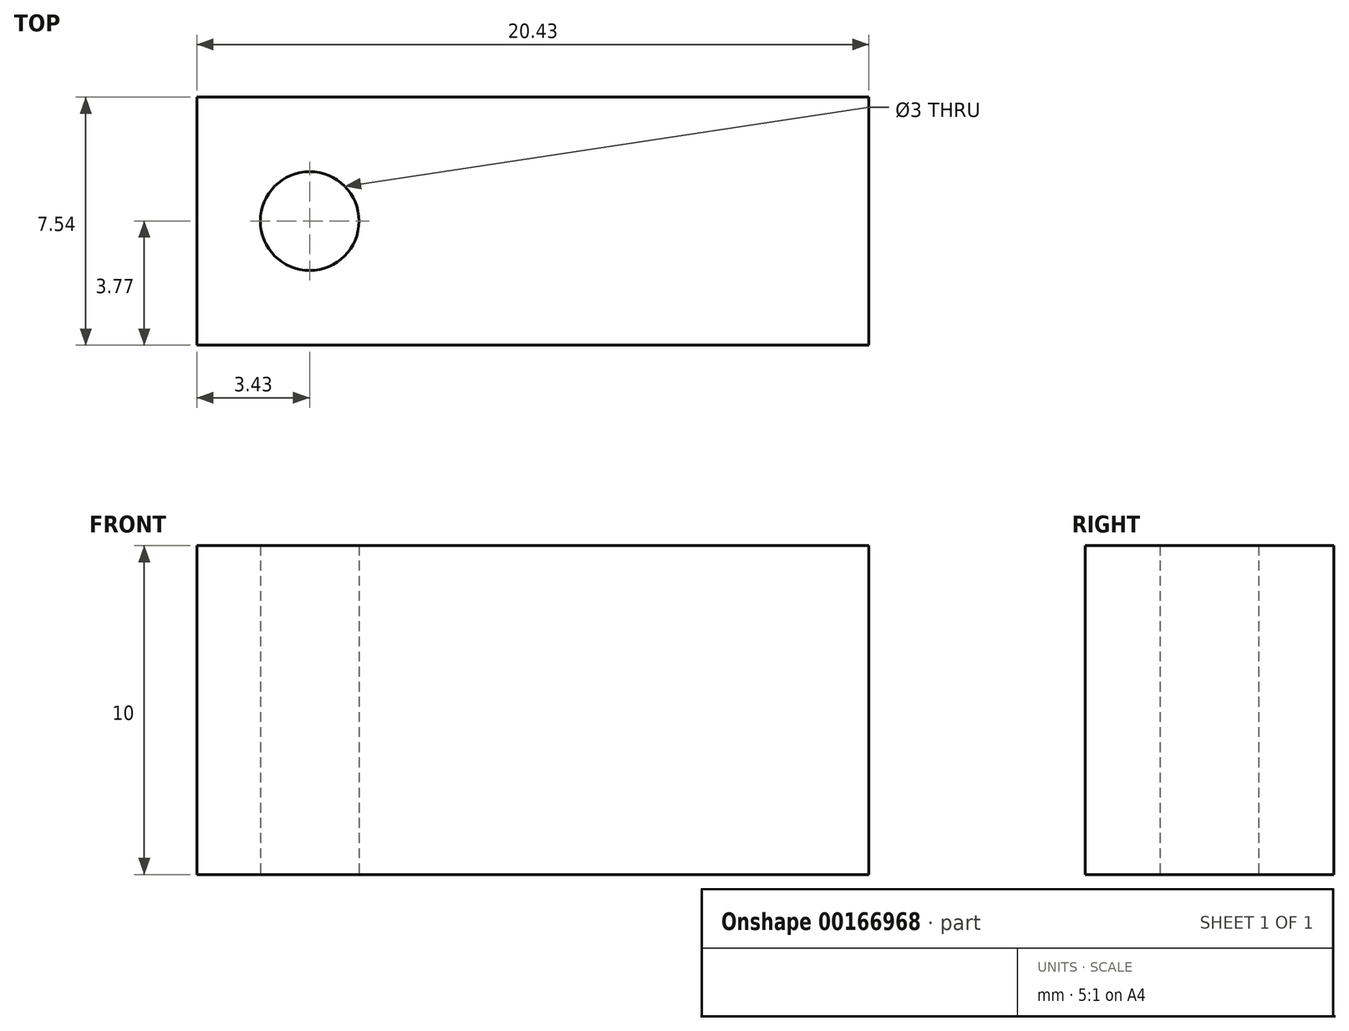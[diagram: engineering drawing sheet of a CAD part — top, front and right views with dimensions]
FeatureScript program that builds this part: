
annotation { "Feature Type Name" : "Feature", "Feature Type Description" : "" }
export const myFeature = defineFeature(function(context is Context, id is Id, definition is map)
    precondition{}
    {
        {
            var Q0;
            Q0=qCreatedBy(makeId("Top.planeOp"),FACE);
            var sketch = newSketch(context, id + "F0", { "sketchPlane" : qUnion([Q0])});
            skLineSegment(sketch, "E0.bottom", {"start": v(-3.43, 3.77) * mm, "end": v(17, 3.77) * mm});
            skLineSegment(sketch, "E0.top", {"start": v(-3.43, -3.77) * mm, "end": v(17, -3.77) * mm});
            skLineSegment(sketch, "E0.left", {"start": v(-3.43, 3.77) * mm, "end": v(-3.43, -3.77) * mm});
            skLineSegment(sketch, "E0.right", {"start": v(17, 3.77) * mm, "end": v(17, -3.77) * mm});
            skLineSegment(sketch, "E1", {"start": v(-3.43, 0) * mm, "end": v(17, 0) * mm, "construction": true});
            skCircle(sketch, "E2", {"center": v(0, 0) * mm, "radius": 1.5 * mm});
            skSolve(sketch);
        }
        {
            var Q0;
            Q0=makeQuery(id+"F0.imprint","IMPRINT",FACE,{"disambiguationData":[TD([[makeQuery(id+"F0.imprint","IMPRINT",EDGE,{"derivedFrom":sQuery(id+"F0.wireOp",EDGE,"E0.bottom")}),-1.0]])]});
            extrude(context, id + "F1", {"entities" : qUnion([Q0]), "depth" : 10 * mm});
        }
    });
